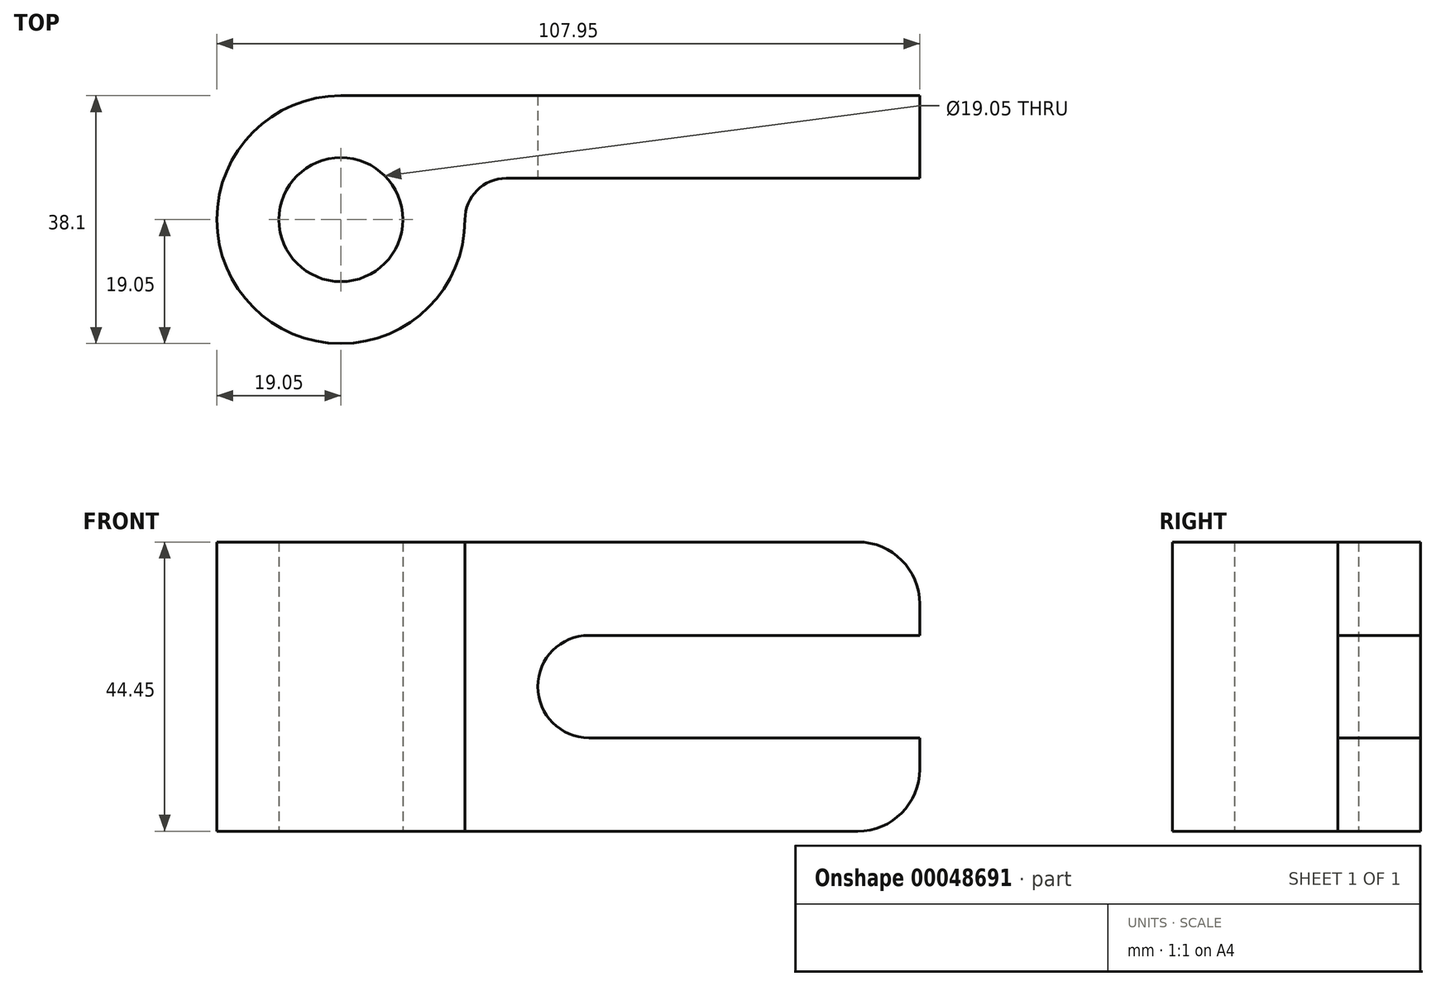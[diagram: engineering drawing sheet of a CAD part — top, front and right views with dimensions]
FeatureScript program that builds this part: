
annotation { "Feature Type Name" : "Feature", "Feature Type Description" : "" }
export const myFeature = defineFeature(function(context is Context, id is Id, definition is map)
    precondition{}
    {
        {
            var Q0;
            Q0=qCreatedBy(makeId("Top.planeOp"),FACE);
            var sketch = newSketch(context, id + "F0", { "sketchPlane" : qUnion([Q0])});
            skCircle(sketch, "E0", {"center": v(0, 0) * mm, "radius": 9.53 * mm});
            skArc(sketch, "E1.0", {"start": v(0, 19.05) * mm, "mid": v(-13.47, -13.47) * mm, "end": v(19.05, 0) * mm});
            skLineSegment(sketch, "E2", {"start": v(0, 19.05) * mm, "end": v(88.9, 19.05) * mm});
            skLineSegment(sketch, "E3", {"start": v(88.9, 19.05) * mm, "end": v(88.9, 6.35) * mm});
            skPoint(sketch, "E4.orphan", {"position": v(88.9, -21.62) * mm});
            skPoint(sketch, "E5.start.orphan", {"position": v(0, -19.05) * mm});
            skLineSegment(sketch, "E6.0", {"start": v(19.05, 6.35) * mm, "end": v(88.9, 6.35) * mm});
            skPoint(sketch, "E7.orphan", {"position": v(88.9, -19.05) * mm});
            skLineSegment(sketch, "E8", {"start": v(19.05, 0) * mm, "end": v(19.05, 6.35) * mm});
            skSolve(sketch);
        }
        {
            var Q0;
            Q0=makeQuery(id+"F0.imprint","IMPRINT",FACE,{"disambiguationData":[TD([[makeQuery(id+"F0.imprint","IMPRINT",EDGE,{"derivedFrom":sQuery(id+"F0.wireOp",EDGE,"E0")}),-1.0]])]});
            extrude(context, id + "F1", {"entities" : qUnion([Q0]), "depth" : 44.45 * mm});
        }
        {
            var Q0;
            Q0=makeQuery(id+"F1.opExtrude","SWEPT_FACE",FACE,{"disambiguationData":[OSD([sQuery(id+"F0.wireOp",EDGE,"E6.0")])]});
            var sketch = newSketch(context, id + "F2", { "sketchPlane" : qUnion([Q0])});
            skArc(sketch, "E9", {"start": v(38.1, 30.1) * mm, "mid": v(30.23, 22.23) * mm, "end": v(38.1, 14.35) * mm});
            skLineSegment(sketch, "E10", {"start": v(38.1, 30.1) * mm, "end": v(88.9, 30.1) * mm});
            skLineSegment(sketch, "E11", {"start": v(38.1, 14.35) * mm, "end": v(88.9, 14.35) * mm});
            skLineSegment(sketch, "E12", {"start": v(88.9, 30.1) * mm, "end": v(88.9, 14.35) * mm});
            skSolve(sketch);
        }
        {
            var Q0;
            Q0=makeQuery(id+"F2.imprint","IMPRINT",FACE,{"disambiguationData":[TD([[makeQuery(id+"F2.imprint","IMPRINT",EDGE,{"derivedFrom":sQuery(id+"F2.wireOp",EDGE,"E9")}),1.0]])]});
            extrude(context, id + "F3", {"entities" : qUnion([Q0]), "operationType" : NewBodyOperationType.REMOVE, "endBound" : BoundingType.THROUGH_ALL, "oppositeDirection" : true, "depth" : 25.4 * mm});
        }
        {
            var Q0;
            Q0=makeQuery(id+"F1.opExtrude","SWEPT_EDGE",EDGE,{"disambiguationData":[OSD([sQuery(id+"F0.wireOp",EDGE,"E6.0"),sQuery(id+"F0.wireOp",EDGE,"E8")])]});
            fillet(context, id + "F4", {"entities" : qUnion([Q0]), "radius" : 6.35 * mm, "allowEdgeOverflow" : false});
        }
        {
            var Q0;
            Q0=makeQuery(id+"F1.opExtrude","CAP_EDGE",EDGE,{"disambiguationData":[OSD([sQuery(id+"F0.wireOp",EDGE,"E3")])],"isStart":true});
            var Q1;
            Q1=makeQuery(id+"F1.opExtrude","CAP_EDGE",EDGE,{"disambiguationData":[OSD([sQuery(id+"F0.wireOp",EDGE,"E3")])],"isStart":false});
            fillet(context, id + "F5", {"entities" : qUnion([Q0, Q1]), "radius" : 9.52 * mm, "allowEdgeOverflow" : false});
        }
    });
